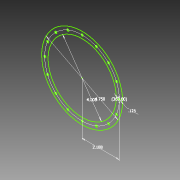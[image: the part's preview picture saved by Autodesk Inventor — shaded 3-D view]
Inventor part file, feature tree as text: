
AUTODESK INVENTOR PART (.ipt)
format: ipt  version: 2015 SP1 (Build 190203100, 203)  size: 72,192 bytes
history: native  units: in
note: dims shown in document units (in); Inventor stores cm internally (conversion verified against a paired STEP export)
features: sketch x1
ambient origin geometry x8: Origin, YZ Plane, XZ Plane, XY Plane, X Axis, Y Axis, Z Axis, Center Point
feature tree (1):
  sketch  "Sketch1"  dims[d0=4.75in d1=4.0in d2=0.125in d3=2.1875in d4=6.2992in d6=360.0deg]
